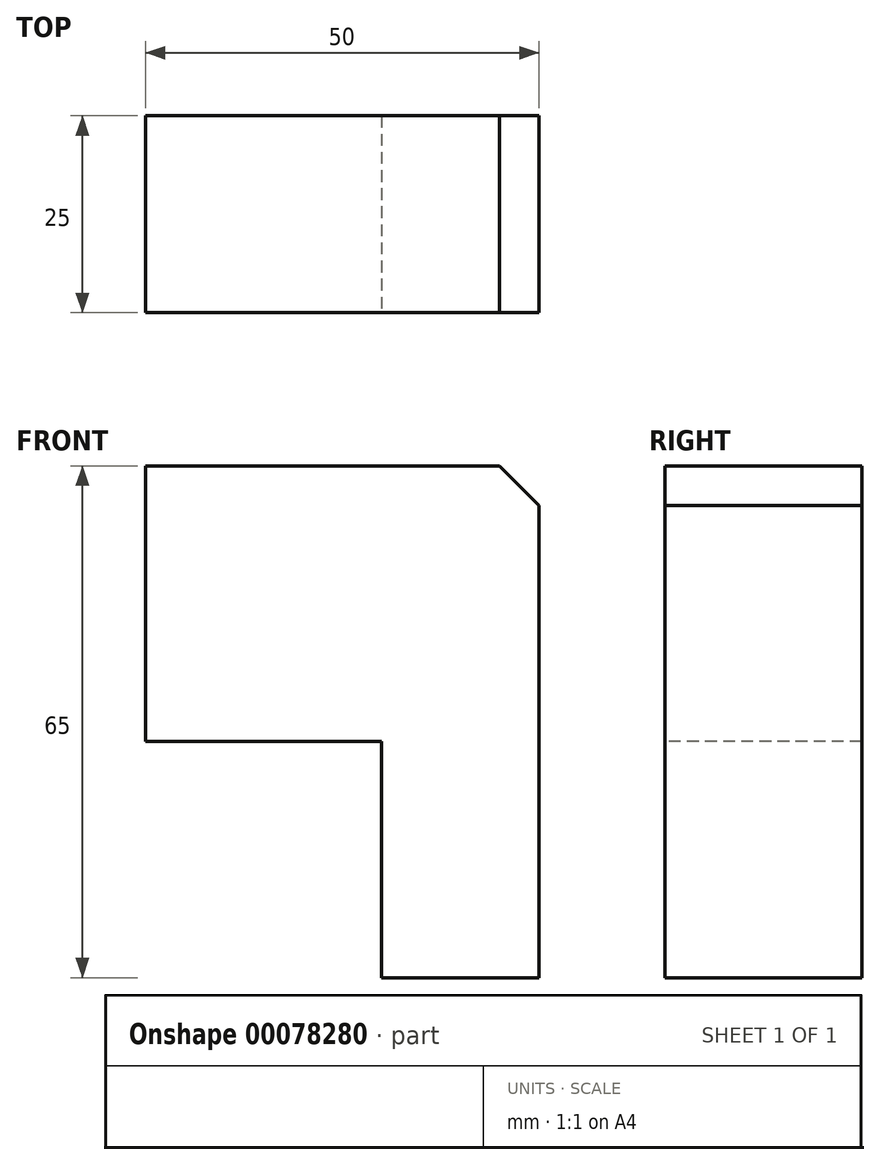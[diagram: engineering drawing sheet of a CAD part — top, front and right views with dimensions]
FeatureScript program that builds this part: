
annotation { "Feature Type Name" : "Feature", "Feature Type Description" : "" }
export const myFeature = defineFeature(function(context is Context, id is Id, definition is map)
    precondition{}
    {
        {
            var Q0;
            Q0=qCreatedBy(makeId("Front.planeOp"),FACE);
            var sketch = newSketch(context, id + "F4", { "sketchPlane" : qUnion([Q0])});
            skLineSegment(sketch, "E0.bottom", {"start": v(20, 39.96) * mm, "end": v(-30, 39.96) * mm});
            skLineSegment(sketch, "E0.top", {"start": v(20, -25.04) * mm, "end": v(-30, -25.04) * mm});
            skLineSegment(sketch, "E0.left", {"start": v(20, 39.96) * mm, "end": v(20, -25.04) * mm});
            skLineSegment(sketch, "E0.right", {"start": v(-30, 39.96) * mm, "end": v(-30, -25.04) * mm});
            skSolve(sketch);
        }
        {
            var Q0;
            Q0=makeQuery(id+"F4.imprint","IMPRINT",FACE,{"disambiguationData":[TD([[makeQuery(id+"F4.imprint","IMPRINT",EDGE,{"derivedFrom":sQuery(id+"F4.wireOp",EDGE,"E0.bottom")}),1.0]])]});
            extrude(context, id + "F0", {"entities" : qUnion([Q0]), "depth" : 25 * mm});
        }
        {
            var Q0;
            Q0=makeQuery(id+"F0.opExtrude","CAP_FACE",FACE,{"disambiguationData":[OSD([sQuery(id+"F4.wireOp",EDGE,"E0.bottom"),sQuery(id+"F4.wireOp",EDGE,"E0.top"),sQuery(id+"F4.wireOp",EDGE,"E0.left"),sQuery(id+"F4.wireOp",EDGE,"E0.right")])],"isStart":false});
            var sketch = newSketch(context, id + "F1", { "sketchPlane" : qUnion([Q0])});
            skLineSegment(sketch, "E1.bottom", {"start": v(0, 4.96) * mm, "end": v(-40, 4.96) * mm});
            skLineSegment(sketch, "E1.top", {"start": v(0, -30.14) * mm, "end": v(-40, -30.14) * mm});
            skLineSegment(sketch, "E1.left", {"start": v(0, 4.96) * mm, "end": v(0, -30.14) * mm});
            skLineSegment(sketch, "E1.right", {"start": v(-40, 4.96) * mm, "end": v(-40, -30.14) * mm});
            skSolve(sketch);
        }
        {
            var Q0;
            {var subQ0=sQuery(id+"F1.wireOp",EDGE,"E1.left");var subQ1=sQuery(id+"F1.wireOp",EDGE,"E1.bottom");var subQ2=makeQuery(id+"F1.imprint","INTERSECT",VERTEX,{"derivedFrom":[subQ1,subQ0]});Q0=makeQuery(id+"F1.imprint","IMPRINT",FACE,{"disambiguationData":[TD([[makeQuery(id+"F1.imprint","IMPRINT",EDGE,{"disambiguationData":[TD([[subQ2,-1.0]])],"derivedFrom":subQ1}),1.0]])]});}
            extrude(context, id + "F2", {"entities" : qUnion([Q0]), "operationType" : NewBodyOperationType.REMOVE, "oppositeDirection" : true, "depth" : 25 * mm});
        }
        {
            var Q0;
            Q0=makeQuery(id+"F0.opExtrude","SWEPT_EDGE",EDGE,{"disambiguationData":[OSD([sQuery(id+"F4.wireOp",EDGE,"E0.bottom"),sQuery(id+"F4.wireOp",EDGE,"E0.left")])]});
            chamfer(context, id + "F3", {"entities" : qUnion([Q0]), "width" : 5 * mm, "tangentPropagation" : true});
        }
    });
